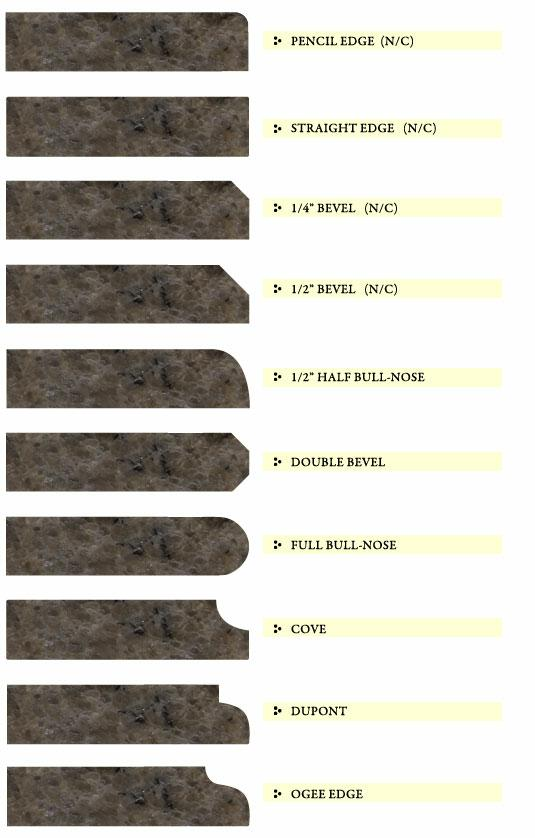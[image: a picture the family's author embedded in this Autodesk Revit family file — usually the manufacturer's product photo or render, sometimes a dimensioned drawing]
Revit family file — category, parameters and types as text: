
# Revit family: Casework-DuPont-Zodiaq-_L_-Countertop
name_source: partatom
category: Casework
revit_build: Autodesk Revit Architecture 2015 (Build: 20140903_1530(x64)
units: mm (PartAtom-declared; Revit-internal decimal feet)

## types (2) — shared parameters
1 2 Bevel = No
1 2 Half Bull Nose = No
1 4 Bevel = No
12B = No
12H = No
14B = No
C = No
Cove = No
D = No
DB = No
Description = Quartz Surface Countertop
Double Bevel = No
Dupont = No
FBN = No
Full Bull Nose = No
Height = 3' - 0"
Manufacturer = DuPont
Model = Zodiaq®
OE = No
Ogee Edge = No
PE = No
Pencil Edge = No
Product Name = Zodiaq®
Product Page URL = http://www.dupont.com
SE = Yes
Straight Edge = Yes
zero-valued in all types: Cost

## per-type parameters (varying)
| type | Countertop Material | Depth | Thickness | URL |
| 2cm | Quartz Surface - DuPont - Zodiaq - Névé 2cm | 2' - 0" | 0' - 0 3/4" | www.zodiaq.com |
| 3cm | Quartz Surface - DuPont - Zodiaq - Névé 3cm | 2' - 6" | 0' - 1 3/16" | http://www.dupont.com |

## geometry (parser evidence)
native form markers: Sweep x15
no freeform markers — native parametric forms only
